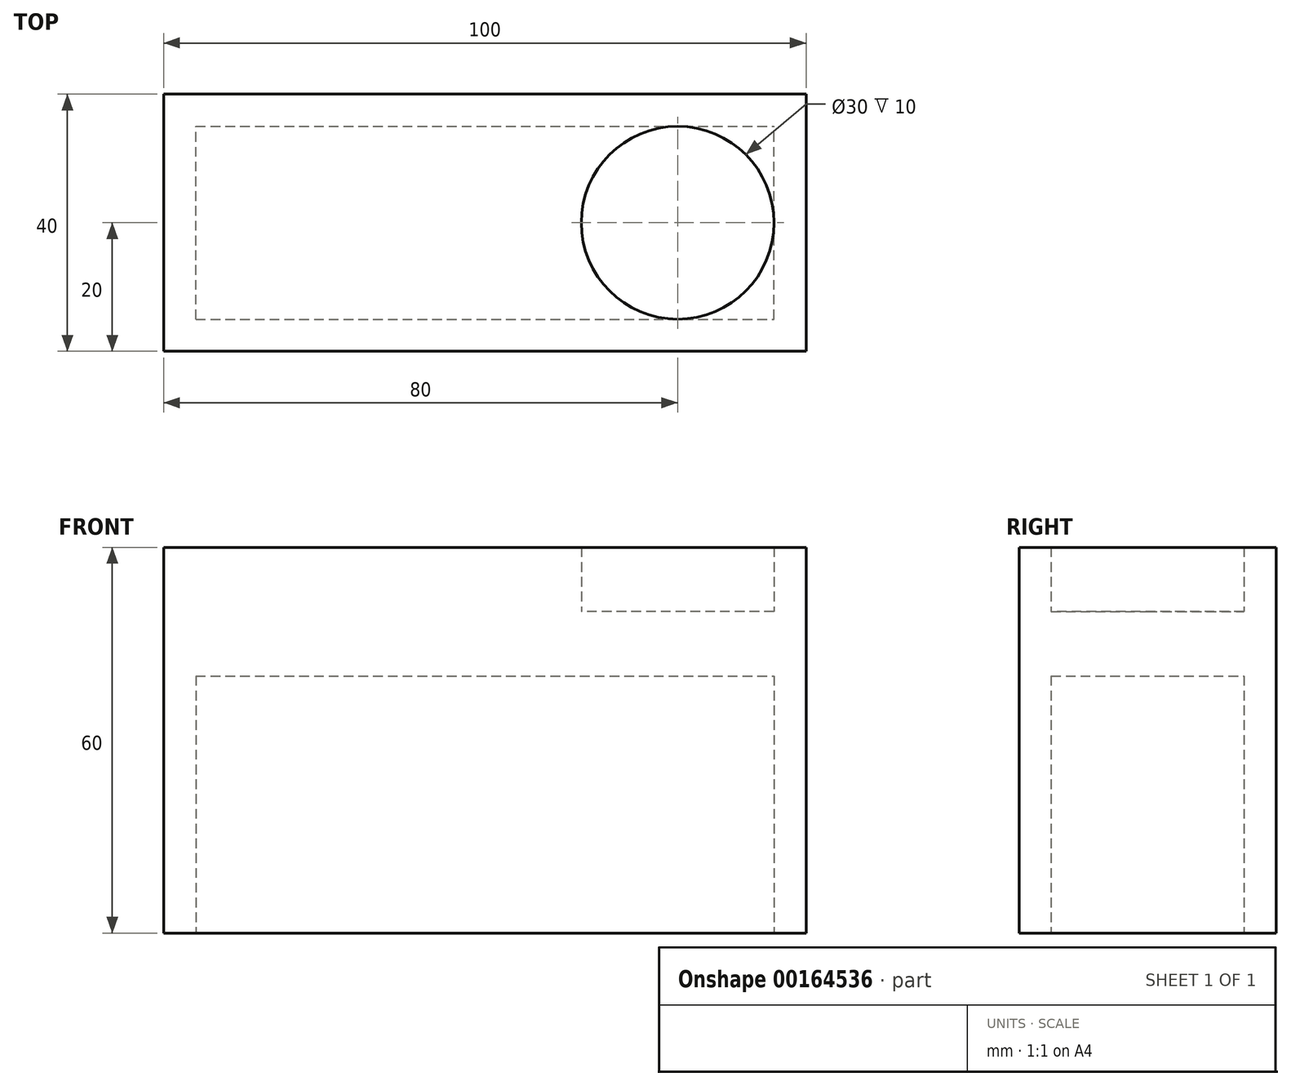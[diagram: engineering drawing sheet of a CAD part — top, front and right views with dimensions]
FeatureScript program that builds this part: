
annotation { "Feature Type Name" : "Feature", "Feature Type Description" : "" }
export const myFeature = defineFeature(function(context is Context, id is Id, definition is map)
    precondition{}
    {
        {
            var Q0;
            Q0=qCreatedBy(makeId("Top.planeOp"),FACE);
            var sketch = newSketch(context, id + "F0", { "sketchPlane" : qUnion([Q0])});
            skLineSegment(sketch, "E0.bottom", {"start": v(50, -20) * mm, "end": v(-50, -20) * mm});
            skLineSegment(sketch, "E0.top", {"start": v(50, 20) * mm, "end": v(-50, 20) * mm});
            skLineSegment(sketch, "E0.left", {"start": v(50, -20) * mm, "end": v(50, 20) * mm});
            skLineSegment(sketch, "E0.right", {"start": v(-50, -20) * mm, "end": v(-50, 20) * mm});
            skPoint(sketch, "E0.middle", {"position": v(0, 0) * mm});
            skSolve(sketch);
        }
        {
            var Q0;
            Q0 = qSketchRegion(id + "F0", true);
            extrude(context, id + "F1", {"entities" : qUnion([Q0]), "depth" : 50 * mm});
        }
        {
            var Q0;
            Q0=makeQuery(id+"F1.opExtrude","CAP_FACE",FACE,{"disambiguationData":[OSD([sQuery(id+"F0.wireOp",EDGE,"E0.bottom"),sQuery(id+"F0.wireOp",EDGE,"E0.top"),sQuery(id+"F0.wireOp",EDGE,"E0.left"),sQuery(id+"F0.wireOp",EDGE,"E0.right")])],"isStart":false});
            var sketch = newSketch(context, id + "F2", { "sketchPlane" : qUnion([Q0])});
            skCircle(sketch, "E1", {"center": v(-30, 0) * mm, "radius": 15 * mm});
            skPoint(sketch, "E1.centerSnap0", {"position": v(-50, 0) * mm});
            skCircle(sketch, "E2.MirrorC", {"center": v(30, 0) * mm, "radius": 15 * mm});
            skSolve(sketch);
        }
        {
            var Q0;
            Q0=makeQuery(id+"F2.imprint","IMPRINT",FACE,{"disambiguationData":[TD([[makeQuery(id+"F2.imprint","IMPRINT",EDGE,{"derivedFrom":sQuery(id+"F2.wireOp",EDGE,"E1")}),1.0]])]});
            var Q1;
            Q1=makeQuery(id+"F2.imprint","IMPRINT",FACE,{"disambiguationData":[TD([[makeQuery(id+"F2.imprint","IMPRINT",EDGE,{"derivedFrom":sQuery(id+"F2.wireOp",EDGE,"E2.MirrorC")}),-1.0]])]});
            extrude(context, id + "F3", {"entities" : qUnion([Q0, Q1]), "operationType" : NewBodyOperationType.ADD, "depth" : 10 * mm});
        }
        {
            var Q0;
            Q0=makeQuery(id+"F1.opExtrude","CAP_FACE",FACE,{"disambiguationData":[OSD([sQuery(id+"F0.wireOp",EDGE,"E0.bottom"),sQuery(id+"F0.wireOp",EDGE,"E0.top"),sQuery(id+"F0.wireOp",EDGE,"E0.left"),sQuery(id+"F0.wireOp",EDGE,"E0.right")])],"isStart":true});
            var sketch = newSketch(context, id + "F4", { "sketchPlane" : qUnion([Q0])});
            skLineSegment(sketch, "E3.bottom", {"start": v(-45, 15) * mm, "end": v(45, 15) * mm});
            skLineSegment(sketch, "E3.top", {"start": v(-45, -15) * mm, "end": v(45, -15) * mm});
            skLineSegment(sketch, "E3.left", {"start": v(-45, 15) * mm, "end": v(-45, -15) * mm});
            skLineSegment(sketch, "E3.right", {"start": v(45, 15) * mm, "end": v(45, -15) * mm});
            skPoint(sketch, "E3.middle", {"position": v(0, 0) * mm});
            skSolve(sketch);
        }
        {
            var Q0;
            Q0=makeQuery(id+"F4.imprint","IMPRINT",FACE,{"disambiguationData":[TD([[makeQuery(id+"F4.imprint","IMPRINT",EDGE,{"derivedFrom":sQuery(id+"F4.wireOp",EDGE,"E3.bottom")}),-1.0]])]});
            extrude(context, id + "F5", {"entities" : qUnion([Q0]), "operationType" : NewBodyOperationType.REMOVE, "oppositeDirection" : true, "depth" : 40 * mm});
        }
    });
